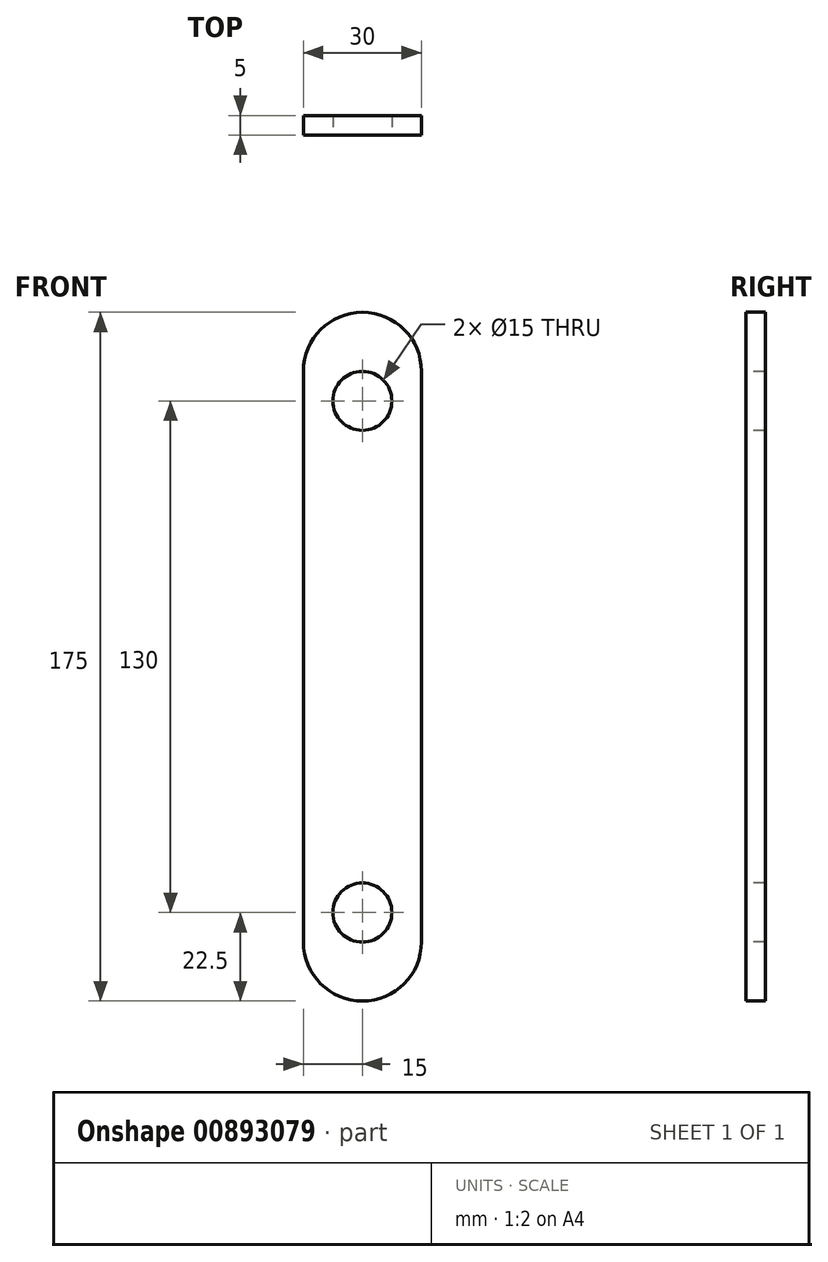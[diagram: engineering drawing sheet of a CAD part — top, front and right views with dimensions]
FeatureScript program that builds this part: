
annotation { "Feature Type Name" : "Feature", "Feature Type Description" : "" }
export const myFeature = defineFeature(function(context is Context, id is Id, definition is map)
    precondition{}
    {
        {
            var Q0;
            Q0=qCreatedBy(makeId("Front.planeOp"),FACE);
            var sketch = newSketch(context, id + "F0", { "sketchPlane" : qUnion([Q0])});
            skArc(sketch, "E0", {"start": v(15, 72.5) * mm, "mid": v(0, 87.5) * mm, "end": v(-15, 72.5) * mm});
            skArc(sketch, "E1", {"start": v(-15, -72.5) * mm, "mid": v(0, -87.5) * mm, "end": v(15, -72.5) * mm});
            skLineSegment(sketch, "E2", {"start": v(-15, 72.5) * mm, "end": v(-15, -72.5) * mm});
            skLineSegment(sketch, "E3", {"start": v(15, 72.5) * mm, "end": v(15, -72.5) * mm});
            skSolve(sketch);
        }
        {
            var Q0;
            Q0 = qSketchRegion(id + "F0", true);
            extrude(context, id + "F1", {"entities" : qUnion([Q0]), "depth" : 5 * mm, "offsetDistance" : 25 * mm});
        }
        {
            var Q0;
            Q0=makeQuery(id+"F1.opExtrude","CAP_FACE",FACE,{"disambiguationData":[OSD([sQuery(id+"F0.wireOp",EDGE,"E0"),sQuery(id+"F0.wireOp",EDGE,"E1"),sQuery(id+"F0.wireOp",EDGE,"E2"),sQuery(id+"F0.wireOp",EDGE,"E3")])],"isStart":false});
            var sketch = newSketch(context, id + "F2", { "sketchPlane" : qUnion([Q0])});
            skCircle(sketch, "E4", {"center": v(0, 65) * mm, "radius": 7.5 * mm});
            skCircle(sketch, "E5", {"center": v(0, -65) * mm, "radius": 7.5 * mm});
            skSolve(sketch);
        }
        {
            var Q0;
            Q0 = qSketchRegion(id + "F2", true);
            extrude(context, id + "F3", {"entities" : qUnion([Q0]), "operationType" : NewBodyOperationType.REMOVE, "oppositeDirection" : true, "depth" : 25 * mm, "offsetDistance" : 25 * mm});
        }
    });
